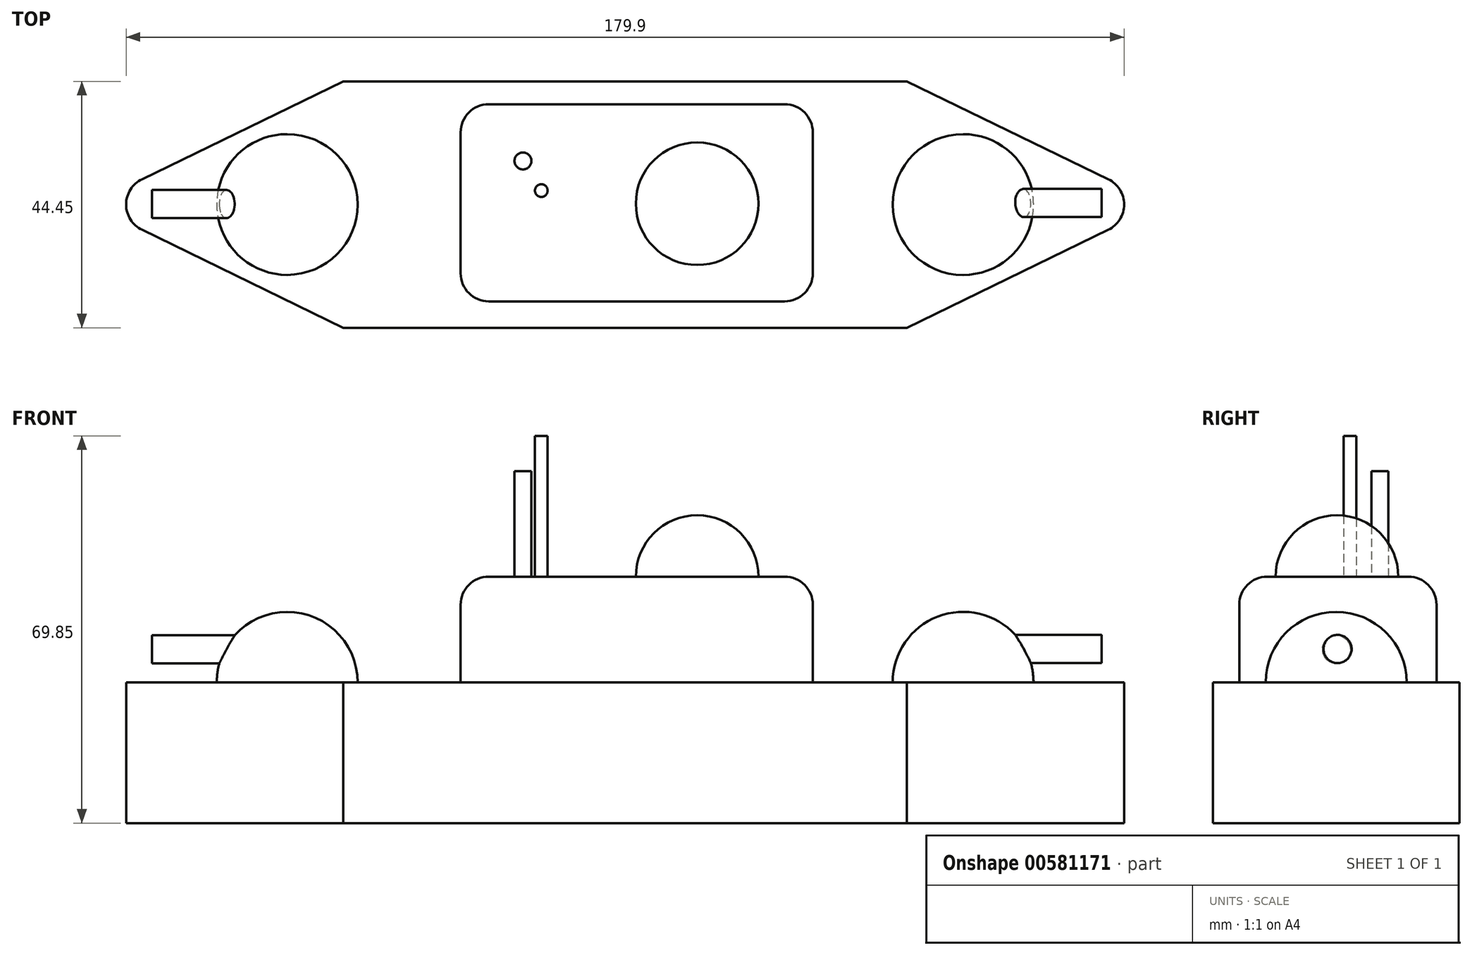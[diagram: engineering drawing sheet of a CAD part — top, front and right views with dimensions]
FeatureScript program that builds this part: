
annotation { "Feature Type Name" : "Feature", "Feature Type Description" : "" }
export const myFeature = defineFeature(function(context is Context, id is Id, definition is map)
    precondition{}
    {
        {
            var Q0;
            Q0=qCreatedBy(makeId("Top.planeOp"),FACE);
            var sketch = newSketch(context, id + "F0", { "sketchPlane" : qUnion([Q0])});
            skLineSegment(sketch, "E0.bottom", {"start": v(-63.8, -30.1) * mm, "end": v(37.8, -30.1) * mm});
            skLineSegment(sketch, "E0.top", {"start": v(-63.8, 14.36) * mm, "end": v(37.8, 14.36) * mm});
            skLineSegment(sketch, "E1", {"start": v(-63.8, 14.36) * mm, "end": v(-109.47, -7.87) * mm});
            skLineSegment(sketch, "E2", {"start": v(-109.47, -7.87) * mm, "end": v(-63.8, -30.1) * mm});
            skLineSegment(sketch, "E3", {"start": v(37.8, 14.36) * mm, "end": v(83.49, -7.87) * mm});
            skLineSegment(sketch, "E4", {"start": v(83.49, -7.87) * mm, "end": v(37.8, -30.1) * mm});
            skSolve(sketch);
        }
        {
            var Q0;
            Q0=makeQuery(id+"F0.imprint","IMPRINT",FACE,{"disambiguationData":[TD([[makeQuery(id+"F0.imprint","IMPRINT",EDGE,{"derivedFrom":sQuery(id+"F0.wireOp",EDGE,"E0.bottom")}),1.0]])]});
            extrude(context, id + "F1", {"entities" : qUnion([Q0]), "depth" : 25.4 * mm, "offsetDistance" : 25.4 * mm});
        }
        {
            var Q0;
            Q0=makeQuery(id+"F1.opExtrude","CAP_FACE",FACE,{"disambiguationData":[OSD([sQuery(id+"F0.wireOp",EDGE,"E0.bottom"),sQuery(id+"F0.wireOp",EDGE,"E0.top"),sQuery(id+"F0.wireOp",EDGE,"E1"),sQuery(id+"F0.wireOp",EDGE,"E2"),sQuery(id+"F0.wireOp",EDGE,"E3"),sQuery(id+"F0.wireOp",EDGE,"E4")])],"isStart":false});
            var sketch = newSketch(context, id + "F2", { "sketchPlane" : qUnion([Q0])});
            skLineSegment(sketch, "E5.bottom", {"start": v(-42.65, 10.22) * mm, "end": v(20.85, 10.22) * mm});
            skLineSegment(sketch, "E5.top", {"start": v(-42.65, -25.34) * mm, "end": v(20.85, -25.34) * mm});
            skLineSegment(sketch, "E5.left", {"start": v(-42.65, 10.22) * mm, "end": v(-42.65, -25.34) * mm});
            skLineSegment(sketch, "E5.right", {"start": v(20.85, 10.22) * mm, "end": v(20.85, -25.34) * mm});
            skSolve(sketch);
        }
        {
            var Q0;
            Q0 = qSketchRegion(id + "F2", true);
            extrude(context, id + "F3", {"entities" : qUnion([Q0]), "operationType" : NewBodyOperationType.ADD, "depth" : 19.05 * mm, "offsetDistance" : 25.4 * mm});
        }
        {
            var Q0;
            Q0=makeQuery(id+"F1.opExtrude","CAP_FACE",FACE,{"disambiguationData":[OSD([sQuery(id+"F0.wireOp",EDGE,"E0.bottom"),sQuery(id+"F0.wireOp",EDGE,"E0.top"),sQuery(id+"F0.wireOp",EDGE,"E1"),sQuery(id+"F0.wireOp",EDGE,"E2"),sQuery(id+"F0.wireOp",EDGE,"E3"),sQuery(id+"F0.wireOp",EDGE,"E4")])],"isStart":false});
            var sketch = newSketch(context, id + "F4", { "sketchPlane" : qUnion([Q0])});
            skArc(sketch, "E6", {"start": v(47.93, 4.83) * mm, "mid": v(35.23, -7.87) * mm, "end": v(47.93, -20.57) * mm});
            skLineSegment(sketch, "E7", {"start": v(47.93, -7.87) * mm, "end": v(47.93, -20.57) * mm});
            skLineSegment(sketch, "E8", {"start": v(47.93, -20.57) * mm, "end": v(47.93, 4.83) * mm});
            skSolve(sketch);
        }
        {
            var Q0;
            {var subQ0=sQuery(id+"F4.wireOp",EDGE,"E6");Q0=makeQuery(id+"F4.imprint","IMPRINT",FACE,{"disambiguationData":[TD([[makeQuery(id+"F4.imprint","IMPRINT",EDGE,{"derivedFrom":subQ0}),-1.0]])]});}
            var sketch = newSketch(context, id + "F5", { "sketchPlane" : qUnion([Q0])});
            skArc(sketch, "E9", {"start": v(-73.9, -20.57) * mm, "mid": v(-61.21, -7.87) * mm, "end": v(-73.9, 4.83) * mm});
            skLineSegment(sketch, "E10", {"start": v(-73.91, -7.87) * mm, "end": v(-73.9, -20.57) * mm});
            skLineSegment(sketch, "E11", {"start": v(-73.9, -20.57) * mm, "end": v(-73.9, 4.83) * mm});
            skSolve(sketch);
        }
        {
            var Q0;
            Q0 = qSketchRegion(id + "F5", true);
            var Q1;
            Q1=sQuery(id+"F5.wireOp",EDGE,"E11");
            revolve(context, id + "F6", {"operationType" : NewBodyOperationType.ADD, "entities" : qUnion([Q0]), "axis" : qUnion([Q1]), "revolveType" : RevolveType.FULL});
        }
        {
            var Q0;
            Q0 = qSketchRegion(id + "F4", true);
            var Q1;
            Q1=sQuery(id+"F4.wireOp",EDGE,"E8");
            revolve(context, id + "F7", {"operationType" : NewBodyOperationType.ADD, "entities" : qUnion([Q0]), "axis" : qUnion([Q1]), "revolveType" : RevolveType.FULL});
        }
        {
            var Q0;
            Q0=qCreatedBy(makeId("Right.planeOp"),FACE);
            cPlane(context, id + "F8", {"entities" : qUnion([Q0]), "cplaneType" : CPlaneType.OFFSET, "offset" : 53.85 * mm, "width" : 152.4 * mm, "height" : 152.4 * mm});
        }
        {
            var Q0;
            Q0=qCreatedBy(id+"F8.planeOp",FACE);
            var sketch = newSketch(context, id + "F9", { "sketchPlane" : qUnion([Q0])});
            skCircle(sketch, "E12", {"center": v(-7.6, 31.4) * mm, "radius": 2.54 * mm});
            skSolve(sketch);
        }
        {
            var Q0;
            Q0 = qSketchRegion(id + "F9", true);
            extrude(context, id + "F10", {"entities" : qUnion([Q0]), "operationType" : NewBodyOperationType.ADD, "depth" : 19.05 * mm, "offsetDistance" : 25.4 * mm});
        }
        {
            var Q0;
            Q0=qCreatedBy(makeId("Right.planeOp"),FACE);
            cPlane(context, id + "F11", {"entities" : qUnion([Q0]), "cplaneType" : CPlaneType.OFFSET, "offset" : 79.25 * mm, "oppositeDirection" : true, "width" : 152.4 * mm, "height" : 152.4 * mm});
        }
        {
            var Q0;
            Q0=qCreatedBy(id+"F11.planeOp",FACE);
            var sketch = newSketch(context, id + "F12", { "sketchPlane" : qUnion([Q0])});
            skCircle(sketch, "E13", {"center": v(-7.78, 31.32) * mm, "radius": 2.54 * mm});
            skSolve(sketch);
        }
        {
            var Q0;
            Q0 = qSketchRegion(id + "F12", true);
            extrude(context, id + "F13", {"entities" : qUnion([Q0]), "operationType" : NewBodyOperationType.ADD, "oppositeDirection" : true, "depth" : 19.05 * mm, "offsetDistance" : 25.4 * mm});
        }
        {
            var Q0;
            Q0=makeQuery(id+"F3.opExtrude","CAP_EDGE",EDGE,{"disambiguationData":[OSD([sQuery(id+"F2.wireOp",EDGE,"E5.left")])],"isStart":false});
            var Q1;
            Q1=makeQuery(id+"F3.opExtrude","CAP_EDGE",EDGE,{"disambiguationData":[OSD([sQuery(id+"F2.wireOp",EDGE,"E5.top")])],"isStart":false});
            var Q2;
            Q2=makeQuery(id+"F3.opExtrude","CAP_EDGE",EDGE,{"disambiguationData":[OSD([sQuery(id+"F2.wireOp",EDGE,"E5.bottom")])],"isStart":false});
            var Q3;
            Q3=makeQuery(id+"F3.opExtrude","CAP_EDGE",EDGE,{"disambiguationData":[OSD([sQuery(id+"F2.wireOp",EDGE,"E5.right")])],"isStart":false});
            var Q4;
            Q4=makeQuery(id+"F3.opExtrude","SWEPT_EDGE",EDGE,{"disambiguationData":[OSD([sQuery(id+"F2.wireOp",EDGE,"E5.top"),sQuery(id+"F2.wireOp",EDGE,"E5.left")])]});
            var Q5;
            Q5=makeQuery(id+"F3.opExtrude","SWEPT_EDGE",EDGE,{"disambiguationData":[OSD([sQuery(id+"F2.wireOp",EDGE,"E5.top"),sQuery(id+"F2.wireOp",EDGE,"E5.right")])]});
            var Q6;
            Q6=makeQuery(id+"F3.opExtrude","SWEPT_EDGE",EDGE,{"disambiguationData":[OSD([sQuery(id+"F2.wireOp",EDGE,"E5.bottom"),sQuery(id+"F2.wireOp",EDGE,"E5.right")])]});
            var Q7;
            Q7=makeQuery(id+"F3.opExtrude","SWEPT_EDGE",EDGE,{"disambiguationData":[OSD([sQuery(id+"F2.wireOp",EDGE,"E5.bottom"),sQuery(id+"F2.wireOp",EDGE,"E5.left")])]});
            fillet(context, id + "F14", {"entities" : qUnion([Q0, Q1, Q2, Q3, Q4, Q5, Q6, Q7]), "radius" : 5.08 * mm, "tangentPropagation" : true, "allowEdgeOverflow" : false});
        }
        {
            var Q0;
            Q0=makeQuery(id+"F1.opExtrude","SWEPT_EDGE",EDGE,{"disambiguationData":[OSD([sQuery(id+"F0.wireOp",EDGE,"E1"),sQuery(id+"F0.wireOp",EDGE,"E2")])]});
            var Q1;
            Q1=makeQuery(id+"F1.opExtrude","SWEPT_EDGE",EDGE,{"disambiguationData":[OSD([sQuery(id+"F0.wireOp",EDGE,"E3"),sQuery(id+"F0.wireOp",EDGE,"E4")])]});
            fillet(context, id + "F15", {"entities" : qUnion([Q0, Q1]), "radius" : 5.08 * mm, "tangentPropagation" : true, "allowEdgeOverflow" : false});
        }
        {
            var Q0;
            Q0=makeQuery(id+"F3.opExtrude","CAP_FACE",FACE,{"disambiguationData":[OSD([sQuery(id+"F2.wireOp",EDGE,"E5.bottom"),sQuery(id+"F2.wireOp",EDGE,"E5.top"),sQuery(id+"F2.wireOp",EDGE,"E5.left"),sQuery(id+"F2.wireOp",EDGE,"E5.right")])],"isStart":false});
            var sketch = newSketch(context, id + "F16", { "sketchPlane" : qUnion([Q0])});
            skCircle(sketch, "E14", {"center": v(-31.41, 0) * mm, "radius": 1.53 * mm});
            skSolve(sketch);
        }
        {
            var Q0;
            Q0 = qSketchRegion(id + "F16", true);
            extrude(context, id + "F17", {"entities" : qUnion([Q0]), "operationType" : NewBodyOperationType.ADD, "depth" : 19.05 * mm, "offsetDistance" : 25.4 * mm});
        }
        {
            var Q0;
            Q0=makeQuery(id+"F3.opExtrude","CAP_FACE",FACE,{"disambiguationData":[OSD([sQuery(id+"F2.wireOp",EDGE,"E5.bottom"),sQuery(id+"F2.wireOp",EDGE,"E5.top"),sQuery(id+"F2.wireOp",EDGE,"E5.left"),sQuery(id+"F2.wireOp",EDGE,"E5.right")])],"isStart":false});
            var sketch = newSketch(context, id + "F18", { "sketchPlane" : qUnion([Q0])});
            skCircle(sketch, "E15", {"center": v(-28.1, -5.35) * mm, "radius": 1.14 * mm});
            skSolve(sketch);
        }
        {
            var Q0;
            Q0 = qSketchRegion(id + "F18", true);
            extrude(context, id + "F19", {"entities" : qUnion([Q0]), "operationType" : NewBodyOperationType.ADD, "depth" : 25.4 * mm, "offsetDistance" : 25.4 * mm});
        }
        {
            var Q0;
            Q0=makeQuery(id+"F3.opExtrude","CAP_FACE",FACE,{"disambiguationData":[OSD([sQuery(id+"F2.wireOp",EDGE,"E5.bottom"),sQuery(id+"F2.wireOp",EDGE,"E5.top"),sQuery(id+"F2.wireOp",EDGE,"E5.left"),sQuery(id+"F2.wireOp",EDGE,"E5.right")])],"isStart":false});
            var sketch = newSketch(context, id + "F20", { "sketchPlane" : qUnion([Q0])});
            skArc(sketch, "E16", {"start": v(0, -18.78) * mm, "mid": v(11.06, -7.72) * mm, "end": v(0, 3.34) * mm});
            skLineSegment(sketch, "E17", {"start": v(0, 3.34) * mm, "end": v(0, -7.72) * mm});
            skLineSegment(sketch, "E18", {"start": v(0, -18.78) * mm, "end": v(0, -7.72) * mm});
            skSolve(sketch);
        }
        {
            var Q0;
            Q0 = qSketchRegion(id + "F20", true);
            var Q1;
            Q1=sQuery(id+"F20.wireOp",EDGE,"E18");
            revolve(context, id + "F21", {"operationType" : NewBodyOperationType.ADD, "entities" : qUnion([Q0]), "axis" : qUnion([Q1]), "revolveType" : RevolveType.FULL});
        }
        {
            var Q0;
            Q0=qCreatedBy(makeId("Right.planeOp"),FACE);
            var sketch = newSketch(context, id + "F22", { "sketchPlane" : qUnion([Q0])});
            skCircle(sketch, "E19", {"center": v(-8.24, 50.67) * mm, "radius": 2.27 * mm});
            skSolve(sketch);
        }
        {
            var Q0;
            Q0=sQuery(id+"F22.wireOp",EDGE,"E19");
            extrude(context, id + "F23", {"bodyType" : ToolBodyType.SURFACE, "surfaceEntities" : qUnion([Q0]), "depth" : 22.86 * mm, "offsetDistance" : 25.4 * mm});
        }
    });
